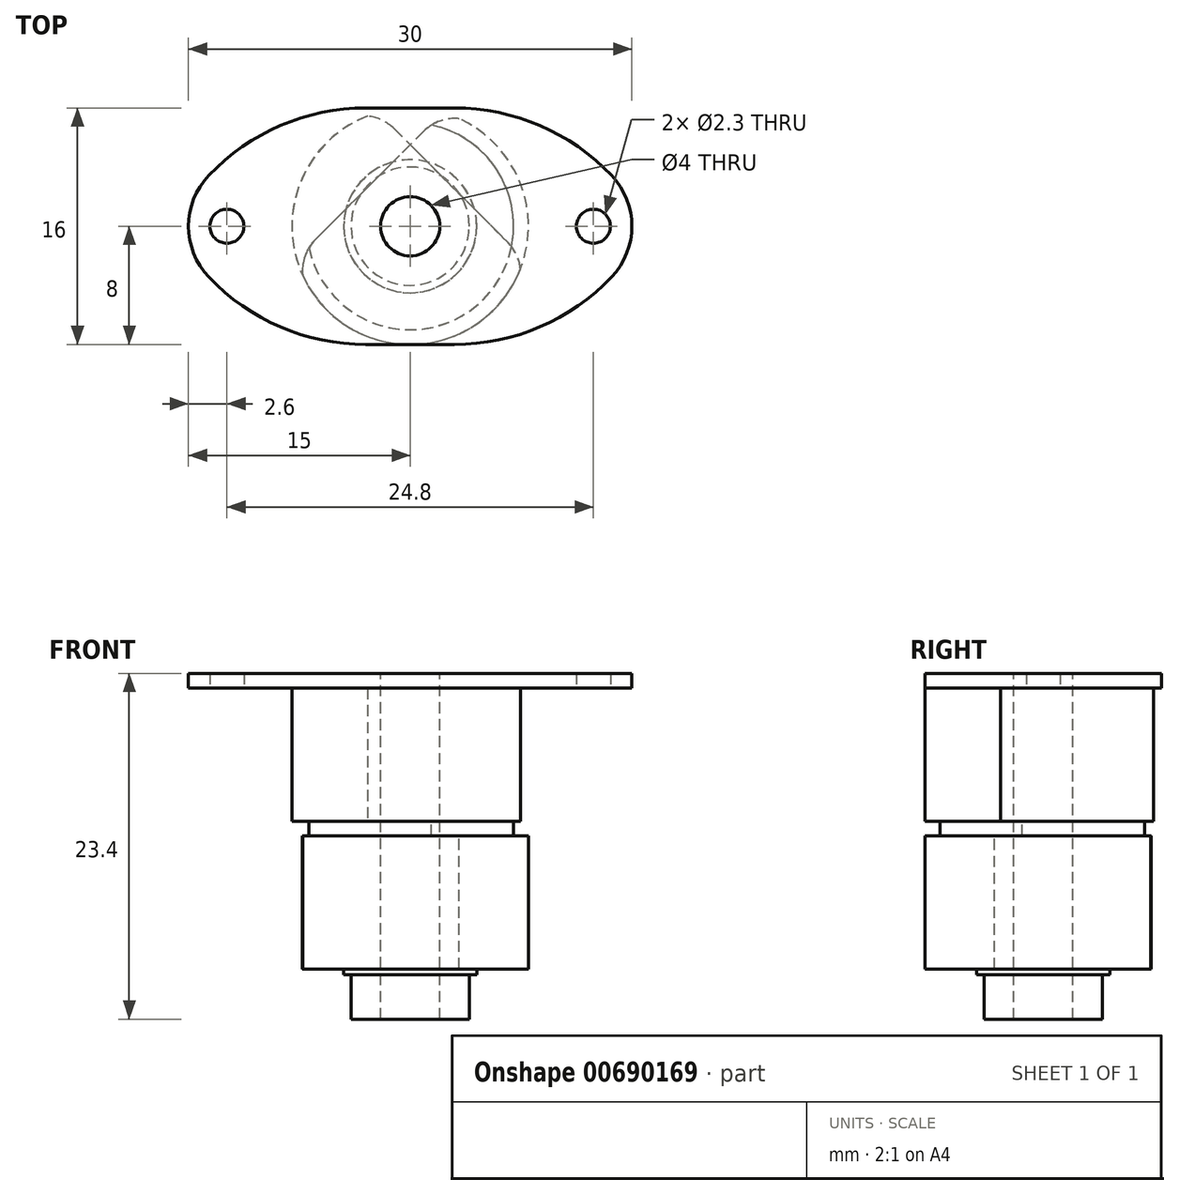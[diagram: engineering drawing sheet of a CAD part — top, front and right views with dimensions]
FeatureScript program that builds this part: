
annotation { "Feature Type Name" : "Feature", "Feature Type Description" : "" }
export const myFeature = defineFeature(function(context is Context, id is Id, definition is map)
    precondition{}
    {
        {
            var Q0;
            Q0=qCreatedBy(makeId("Front.planeOp"),FACE);
            var sketch = newSketch(context, id + "F0", { "sketchPlane" : qUnion([Q0])});
            skLineSegment(sketch, "E0", {"start": v(-2, 22.4) * mm, "end": v(-2, 0) * mm});
            skLineSegment(sketch, "E1", {"start": v(-2, 0) * mm, "end": v(-4, 0) * mm});
            skLineSegment(sketch, "E2", {"start": v(-4.5, 3.4) * mm, "end": v(-8, 3.4) * mm});
            skLineSegment(sketch, "E3", {"start": v(-8, 3.4) * mm, "end": v(-8, 12.4) * mm});
            skLineSegment(sketch, "E4", {"start": v(-8, 12.4) * mm, "end": v(-7, 12.4) * mm});
            skLineSegment(sketch, "E5", {"start": v(-7, 12.4) * mm, "end": v(-7, 13.4) * mm});
            skLineSegment(sketch, "E6", {"start": v(-7, 13.4) * mm, "end": v(-8, 13.4) * mm});
            skLineSegment(sketch, "E7", {"start": v(-8, 13.4) * mm, "end": v(-8, 22.4) * mm});
            skLineSegment(sketch, "E8", {"start": v(-8, 22.4) * mm, "end": v(-2, 22.4) * mm});
            skLineSegment(sketch, "E9", {"start": v(0, 48) * mm, "end": v(0, -30.17) * mm});
            skLineSegment(sketch, "E10", {"start": v(-4.5, 3.4) * mm, "end": v(-4.5, 3) * mm});
            skLineSegment(sketch, "E11", {"start": v(-4.5, 3) * mm, "end": v(-4, 3) * mm});
            skLineSegment(sketch, "E12", {"start": v(-4, 3) * mm, "end": v(-4, 0) * mm});
            skSolve(sketch);
        }
        {
            var Q0;
            Q0 = qSketchRegion(id + "F0", true);
            var Q1;
            Q1=sQuery(id+"F0.wireOp",EDGE,"E9");
            revolve(context, id + "F1", {"entities" : qUnion([Q0]), "axis" : qUnion([Q1]), "revolveType" : RevolveType.FULL});
        }
        {
            var Q0;
            Q0=makeQuery(id+"F1.opRevolve","SWEPT_FACE",FACE,{"disambiguationData":[OSD([sQuery(id+"F0.wireOp",EDGE,"E8")])]});
            var sketch = newSketch(context, id + "F2", { "sketchPlane" : qUnion([Q0])});
            skArc(sketch, "E13", {"start": v(-13.62, 3.45) * mm, "mid": v(-14.64, 1.86) * mm, "end": v(-15, 0) * mm});
            skLineSegment(sketch, "E14", {"start": v(0, 8) * mm, "end": v(0, 0) * mm});
            skLineSegment(sketch, "E15", {"start": v(-15, 0) * mm, "end": v(0, 0) * mm});
            skLineSegment(sketch, "E16", {"start": v(0, 8) * mm, "end": v(-3, 8) * mm});
            skArc(sketch, "E17", {"start": v(-3, 8) * mm, "mid": v(-8.78, 6.81) * mm, "end": v(-13.62, 3.45) * mm});
            skLineSegment(sketch, "E18.MirrorCS", {"start": v(0, -8) * mm, "end": v(-3, -8) * mm});
            skArc(sketch, "E19.MirrorCS", {"start": v(-3, -8) * mm, "mid": v(-8.78, -6.81) * mm, "end": v(-13.62, -3.45) * mm});
            skLineSegment(sketch, "E20.MirrorCS", {"start": v(0, -8) * mm, "end": v(0, 0) * mm});
            skArc(sketch, "E21.MirrorCS", {"start": v(-13.62, -3.45) * mm, "mid": v(-14.64, -1.86) * mm, "end": v(-15, 0) * mm});
            skLineSegment(sketch, "E22.MirrorCS", {"start": v(15, 0) * mm, "end": v(0, 0) * mm});
            skArc(sketch, "E23.MirrorCS", {"start": v(3, -8) * mm, "mid": v(8.78, -6.81) * mm, "end": v(13.62, -3.45) * mm});
            skLineSegment(sketch, "E24.MirrorCS", {"start": v(0, -8) * mm, "end": v(3, -8) * mm});
            skArc(sketch, "E25.MirrorCS", {"start": v(3, 8) * mm, "mid": v(8.78, 6.81) * mm, "end": v(13.62, 3.45) * mm});
            skLineSegment(sketch, "E26.MirrorCS", {"start": v(0, 8) * mm, "end": v(3, 8) * mm});
            skArc(sketch, "E27.MirrorCS", {"start": v(13.62, 3.45) * mm, "mid": v(14.64, 1.86) * mm, "end": v(15, 0) * mm});
            skArc(sketch, "E28.MirrorCS", {"start": v(13.62, -3.45) * mm, "mid": v(14.64, -1.86) * mm, "end": v(15, 0) * mm});
            skSolve(sketch);
        }
        {
            var Q0;
            Q0 = qSketchRegion(id + "F2", true);
            extrude(context, id + "F3", {"entities" : qUnion([Q0]), "operationType" : NewBodyOperationType.ADD, "depth" : 1 * mm, "offsetDistance" : 25 * mm});
        }
        {
            var Q0;
            Q0=makeQuery(id+"F1.opRevolve","SWEPT_FACE",FACE,{"disambiguationData":[OSD([sQuery(id+"F0.wireOp",EDGE,"E6")])]});
            var sketch = newSketch(context, id + "F4", { "sketchPlane" : qUnion([Q0])});
            skArc(sketch, "E29", {"start": v(6.91, 4.95) * mm, "mid": v(-6.01, 6.01) * mm, "end": v(-4.95, -6.91) * mm});
            skCircle(sketch, "E30", {"center": v(0, 0) * mm, "radius": 3.9 * mm, "construction": true});
            skLineSegment(sketch, "E31", {"start": v(-1.08, -6.6) * mm, "end": v(6.6, 1.08) * mm});
            skLineSegment(sketch, "E32", {"start": v(0, -16.17) * mm, "end": v(0, 23.74) * mm, "construction": true});
            skLineSegment(sketch, "E33", {"start": v(2.76, -2.76) * mm, "end": v(0, 0) * mm});
            skArc(sketch, "E34.filletArc", {"start": v(-4.95, -6.91) * mm, "mid": v(-2.95, -7.46) * mm, "end": v(-1.08, -6.6) * mm});
            skArc(sketch, "E35.filletArc", {"start": v(6.6, 1.08) * mm, "mid": v(7.46, 2.95) * mm, "end": v(6.91, 4.95) * mm});
            skCircle(sketch, "E36", {"center": v(0, 0) * mm, "radius": 18.09 * mm});
            skSolve(sketch);
        }
        {
            var Q0;
            Q0 = qSketchRegion(id + "F4", true);
            extrude(context, id + "F5", {"entities" : qUnion([Q0]), "operationType" : NewBodyOperationType.REMOVE, "oppositeDirection" : true, "depth" : 9 * mm, "offsetDistance" : 25 * mm});
        }
        {
            var Q0;
            Q0=qCreatedBy(makeId("Top.planeOp"),FACE);
            var sketch = newSketch(context, id + "F6", { "sketchPlane" : qUnion([Q0])});
            skLineSegment(sketch, "E37", {"start": v(7, 0) * mm, "end": v(-7.72, 0) * mm, "construction": true});
            skCircle(sketch, "E38", {"center": v(12.4, 0) * mm, "radius": 1.15 * mm});
            skCircle(sketch, "E39", {"center": v(-12.4, 0) * mm, "radius": 1.15 * mm});
            skSolve(sketch);
        }
        {
            var Q0;
            Q0 = qSketchRegion(id + "F6", true);
            extrude(context, id + "F7", {"entities" : qUnion([Q0]), "operationType" : NewBodyOperationType.REMOVE, "depth" : 40 * mm, "offsetDistance" : 25 * mm});
        }
        {
            var Q0;
            Q0=makeQuery(id+"F1.opRevolve","SWEPT_FACE",FACE,{"disambiguationData":[OSD([sQuery(id+"F0.wireOp",EDGE,"E6")])]});
            var sketch = newSketch(context, id + "F8", { "sketchPlane" : qUnion([Q0])});
            skArc(sketch, "E40", {"start": v(4.75, -6.75) * mm, "mid": v(5.83, 5.83) * mm, "end": v(-6.75, 4.75) * mm});
            skCircle(sketch, "E41", {"center": v(0, 0) * mm, "radius": 3.9 * mm, "construction": true});
            skCircle(sketch, "E42", {"center": v(0, 0) * mm, "radius": 30 * mm});
            skLineSegment(sketch, "E43", {"start": v(0.9, -6.42) * mm, "end": v(-6.42, 0.9) * mm});
            skLineSegment(sketch, "E44", {"start": v(-2.76, -2.76) * mm, "end": v(0, 0) * mm});
            skLineSegment(sketch, "E45", {"start": v(0, -10.25) * mm, "end": v(0, 17.16) * mm, "construction": true});
            skPoint(sketch, "E46.visualSharp", {"position": v(-7.9, 2.38) * mm});
            skArc(sketch, "E46.filletArc", {"start": v(-6.75, 4.75) * mm, "mid": v(-7.28, 2.76) * mm, "end": v(-6.42, 0.9) * mm});
            skPoint(sketch, "E47.visualSharp", {"position": v(2.38, -7.9) * mm});
            skArc(sketch, "E47.filletArc", {"start": v(0.9, -6.42) * mm, "mid": v(2.76, -7.28) * mm, "end": v(4.75, -6.75) * mm});
            skSolve(sketch);
        }
        {
            var Q0;
            Q0 = qSketchRegion(id + "F8", true);
            extrude(context, id + "F9", {"entities" : qUnion([Q0]), "operationType" : NewBodyOperationType.REMOVE, "depth" : 10 * mm, "offsetDistance" : 25 * mm});
        }
        {
            var Q0;
            Q0=qCreatedBy(makeId("Top.planeOp"),FACE);
            var sketch = newSketch(context, id + "F10", { "sketchPlane" : qUnion([Q0])});
            skCircle(sketch, "E48", {"center": v(0, 0) * mm, "radius": 2 * mm});
            skSolve(sketch);
        }
        {
            var Q0;
            Q0 = qSketchRegion(id + "F10", true);
            extrude(context, id + "F11", {"entities" : qUnion([Q0]), "operationType" : NewBodyOperationType.REMOVE, "depth" : 60 * mm, "offsetDistance" : 25 * mm});
        }
    });
